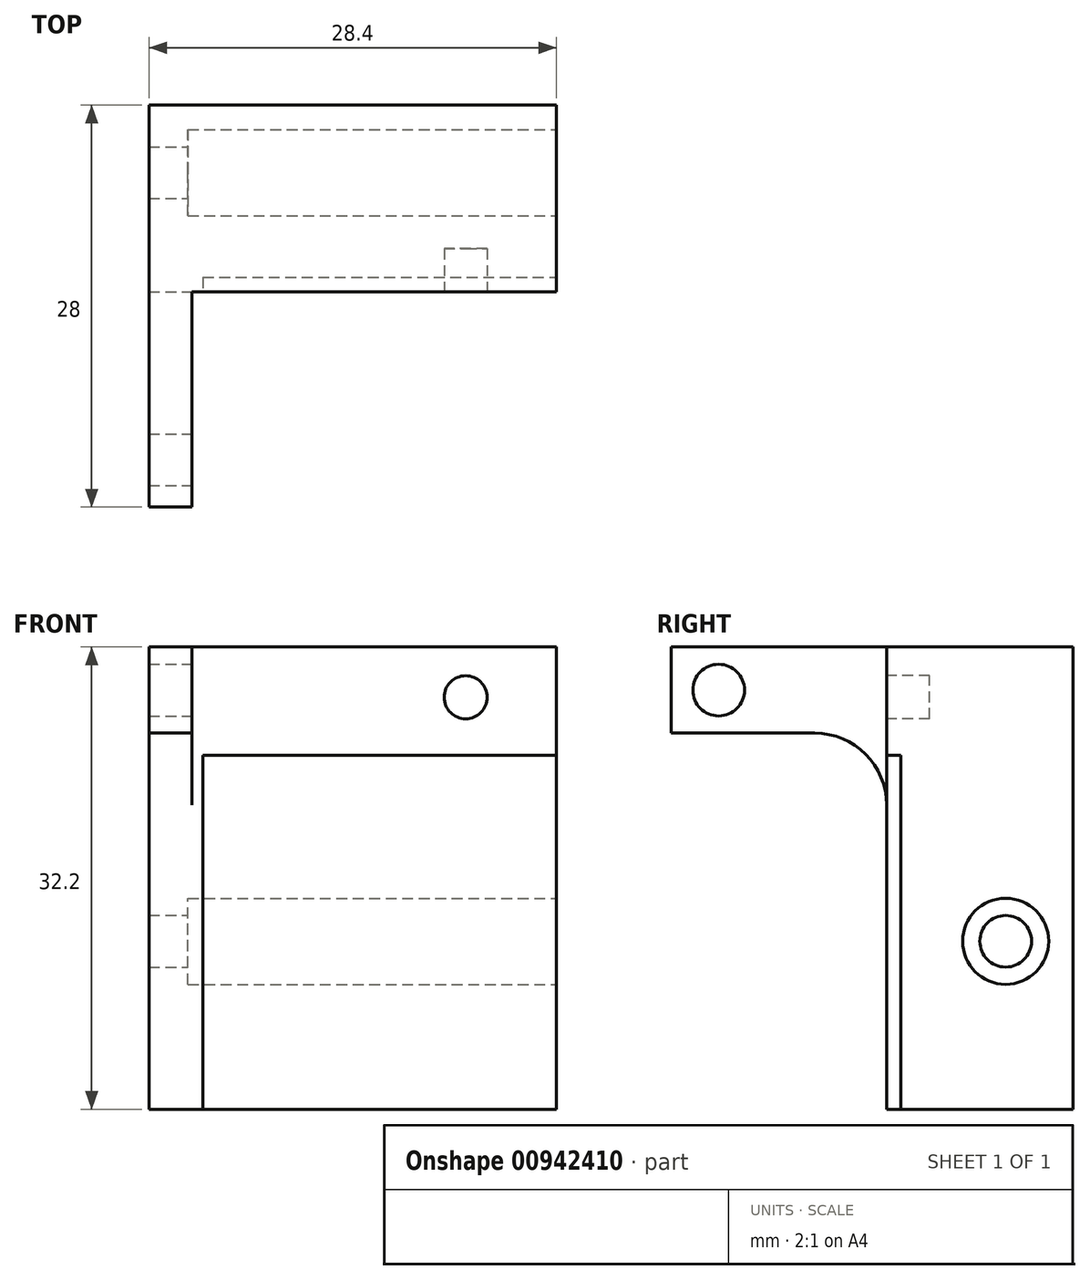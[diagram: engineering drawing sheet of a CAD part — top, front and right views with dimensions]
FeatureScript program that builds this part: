
annotation { "Feature Type Name" : "Feature", "Feature Type Description" : "" }
export const myFeature = defineFeature(function(context is Context, id is Id, definition is map)
    precondition{}
    {
        {
            var Q0;
            Q0=qCreatedBy(makeId("Front.planeOp"),FACE);
            var sketch = newSketch(context, id + "F0", { "sketchPlane" : qUnion([Q0])});
            skLineSegment(sketch, "E0.bottom", {"start": v(-15.2, 13.7) * mm, "end": v(15.2, 13.7) * mm});
            skLineSegment(sketch, "E0.top", {"start": v(-15.2, -13.7) * mm, "end": v(15.2, -13.7) * mm});
            skLineSegment(sketch, "E0.left", {"start": v(-15.2, 13.7) * mm, "end": v(-15.2, -13.7) * mm});
            skLineSegment(sketch, "E0.right", {"start": v(15.2, 13.7) * mm, "end": v(15.2, -13.7) * mm});
            skPoint(sketch, "E0.middle", {"position": v(0, 0) * mm});
            skSolve(sketch);
        }
        {
            var Q0;
            Q0 = qSketchRegion(id + "F0", true);
            extrude(context, id + "F1", {"entities" : qUnion([Q0]), "depth" : 3 * mm, "offsetDistance" : 25 * mm});
        }
        {
            var Q0;
            Q0=makeQuery(id+"F1.opExtrude","CAP_FACE",FACE,{"disambiguationData":[OSD([sQuery(id+"F0.wireOp",EDGE,"E0.bottom"),sQuery(id+"F0.wireOp",EDGE,"E0.top"),sQuery(id+"F0.wireOp",EDGE,"E0.left"),sQuery(id+"F0.wireOp",EDGE,"E0.right")])],"isStart":false});
            var sketch = newSketch(context, id + "F2", { "sketchPlane" : qUnion([Q0])});
            skLineSegment(sketch, "E1.bottom", {"start": v(-11.45, 12.95) * mm, "end": v(14.45, 12.95) * mm});
            skLineSegment(sketch, "E1.top", {"start": v(-11.45, -12.95) * mm, "end": v(14.45, -12.95) * mm});
            skLineSegment(sketch, "E1.left", {"start": v(-11.45, 12.95) * mm, "end": v(-11.45, -12.95) * mm});
            skLineSegment(sketch, "E1.right", {"start": v(14.45, 12.95) * mm, "end": v(14.45, -12.95) * mm});
            skSolve(sketch);
        }
        {
            var Q0;
            Q0 = qSketchRegion(id + "F2", true);
            extrude(context, id + "F3", {"entities" : qUnion([Q0]), "operationType" : NewBodyOperationType.REMOVE, "oppositeDirection" : true, "depth" : 1 * mm, "offsetDistance" : 25 * mm});
        }
        {
            var Q0;
            Q0=makeQuery(id+"F1.opExtrude","CAP_FACE",FACE,{"disambiguationData":[OSD([sQuery(id+"F0.wireOp",EDGE,"E0.bottom"),sQuery(id+"F0.wireOp",EDGE,"E0.top"),sQuery(id+"F0.wireOp",EDGE,"E0.left"),sQuery(id+"F0.wireOp",EDGE,"E0.right")])],"isStart":true});
            var sketch = newSketch(context, id + "F4", { "sketchPlane" : qUnion([Q0])});
            skLineSegment(sketch, "E2.bottom", {"start": v(12.2, 20.5) * mm, "end": v(15.2, 20.5) * mm});
            skLineSegment(sketch, "E2.top", {"start": v(12.2, -20.5) * mm, "end": v(15.2, -20.5) * mm});
            skLineSegment(sketch, "E2.left", {"start": v(12.2, 20.5) * mm, "end": v(12.2, -20.5) * mm});
            skLineSegment(sketch, "E2.right", {"start": v(15.2, 20.5) * mm, "end": v(15.2, -20.5) * mm});
            skSolve(sketch);
        }
        {
            var Q0;
            Q0 = qSketchRegion(id + "F4", true);
            extrude(context, id + "F5", {"entities" : qUnion([Q0]), "operationType" : NewBodyOperationType.ADD, "oppositeDirection" : true, "depth" : 18 * mm, "offsetDistance" : 25 * mm});
        }
        {
            var Q0;
            Q0=makeQuery(id+"F5.opExtrude","SWEPT_FACE",FACE,{"disambiguationData":[OSD([sQuery(id+"F4.wireOp",EDGE,"E2.left")])]});
            var sketch = newSketch(context, id + "F6", { "sketchPlane" : qUnion([Q0])});
            skLineSegment(sketch, "E3.bottom", {"start": v(-18, -14.5) * mm, "end": v(-8, -14.5) * mm});
            skLineSegment(sketch, "E3.top", {"start": v(-18, 14.5) * mm, "end": v(-8, 14.5) * mm});
            skLineSegment(sketch, "E3.left", {"start": v(-18, -14.5) * mm, "end": v(-18, 14.5) * mm});
            skLineSegment(sketch, "E3.right", {"start": v(-3, -9.5) * mm, "end": v(-3, 9.5) * mm});
            skPoint(sketch, "E4.visualSharp", {"position": v(-3, -14.5) * mm});
            skArc(sketch, "E4.filletArc", {"start": v(-8, -14.5) * mm, "mid": v(-4.46, -13.04) * mm, "end": v(-3, -9.5) * mm});
            skPoint(sketch, "E5.visualSharp", {"position": v(-3, 14.5) * mm});
            skArc(sketch, "E5.filletArc", {"start": v(-3, 9.5) * mm, "mid": v(-4.46, 13.04) * mm, "end": v(-8, 14.5) * mm});
            skSolve(sketch);
        }
        {
            var Q0;
            Q0 = qSketchRegion(id + "F6", true);
            extrude(context, id + "F7", {"entities" : qUnion([Q0]), "operationType" : NewBodyOperationType.REMOVE, "oppositeDirection" : true, "depth" : 25 * mm, "offsetDistance" : 25 * mm});
        }
        {
            var Q0;
            Q0=makeQuery(id+"F5.opExtrude","SWEPT_FACE",FACE,{"disambiguationData":[OSD([sQuery(id+"F4.wireOp",EDGE,"E2.left")])]});
            var sketch = newSketch(context, id + "F8", { "sketchPlane" : qUnion([Q0])});
            skCircle(sketch, "E6", {"center": v(-14.7, -17.5) * mm, "radius": 1.8 * mm});
            skPoint(sketch, "E6.centerSnap0", {"position": v(-18, -17.5) * mm});
            skCircle(sketch, "E7", {"center": v(-14.7, 17.5) * mm, "radius": 1.8 * mm});
            skPoint(sketch, "E7.centerSnap0", {"position": v(-18, 17.5) * mm});
            skSolve(sketch);
        }
        {
            var Q0;
            Q0 = qSketchRegion(id + "F8", true);
            extrude(context, id + "F9", {"entities" : qUnion([Q0]), "operationType" : NewBodyOperationType.REMOVE, "oppositeDirection" : true, "depth" : 25 * mm, "offsetDistance" : 25 * mm});
        }
        {
            var Q0;
            Q0=qCreatedBy(makeId("Front.planeOp"),FACE);
            var sketch = newSketch(context, id + "F10", { "sketchPlane" : qUnion([Q0])});
            skLineSegment(sketch, "E8.bottom", {"start": v(-12.2, 13.7) * mm, "end": v(15.2, 13.7) * mm});
            skLineSegment(sketch, "E8.top", {"start": v(-12.2, 20.5) * mm, "end": v(15.2, 20.5) * mm});
            skLineSegment(sketch, "E8.left", {"start": v(-12.2, 13.7) * mm, "end": v(-12.2, 20.5) * mm});
            skLineSegment(sketch, "E8.right", {"start": v(15.2, 13.7) * mm, "end": v(15.2, 20.5) * mm});
            skPoint(sketch, "E9.centerSnap0", {"position": v(15.2, 17.1) * mm});
            skSolve(sketch);
        }
        {
            var Q0;
            Q0 = qSketchRegion(id + "F10", true);
            extrude(context, id + "F11", {"entities" : qUnion([Q0]), "operationType" : NewBodyOperationType.ADD, "depth" : 3 * mm, "offsetDistance" : 25 * mm});
        }
        {
            var Q0;
            Q0=makeQuery(id+"F11.boolean.opBoolean","MERGE",FACE,{"derivedFrom":[makeQuery(id+"F7.boolean.opBoolean","MERGE",FACE,{"derivedFrom":[makeQuery(id+"F1.opExtrude","CAP_FACE",FACE,{"disambiguationData":[OSD([sQuery(id+"F0.wireOp",EDGE,"E0.bottom"),sQuery(id+"F0.wireOp",EDGE,"E0.top"),sQuery(id+"F0.wireOp",EDGE,"E0.left"),sQuery(id+"F0.wireOp",EDGE,"E0.right")])],"isStart":false})],"fromTools":[makeQuery(id+"F7.opExtrude","SWEPT_FACE",FACE,{"disambiguationData":[OSD([sQuery(id+"F6.wireOp",EDGE,"E3.right")])]})]}),makeQuery(id+"F11.opExtrude","CAP_FACE",FACE,{"disambiguationData":[OSD([sQuery(id+"F10.wireOp",EDGE,"E8.bottom"),sQuery(id+"F10.wireOp",EDGE,"E8.top"),sQuery(id+"F10.wireOp",EDGE,"E8.left"),sQuery(id+"F10.wireOp",EDGE,"E8.right")])],"isStart":false})]});
            var sketch = newSketch(context, id + "F12", { "sketchPlane" : qUnion([Q0])});
            skCircle(sketch, "E10", {"center": v(6.87, 17) * mm, "radius": 1.5 * mm});
            skSolve(sketch);
        }
        {
            var Q0;
            Q0 = qSketchRegion(id + "F12", true);
            extrude(context, id + "F13", {"entities" : qUnion([Q0]), "operationType" : NewBodyOperationType.REMOVE, "endBound" : BoundingType.THROUGH_ALL, "oppositeDirection" : true, "depth" : 62.4 * mm, "offsetDistance" : 25 * mm});
        }
        {
            var Q0;
            Q0=makeQuery(id+"F11.boolean.opBoolean","MERGE",FACE,{"derivedFrom":[makeQuery(id+"F7.boolean.opBoolean","MERGE",FACE,{"derivedFrom":[makeQuery(id+"F1.opExtrude","CAP_FACE",FACE,{"disambiguationData":[OSD([sQuery(id+"F0.wireOp",EDGE,"E0.bottom"),sQuery(id+"F0.wireOp",EDGE,"E0.top"),sQuery(id+"F0.wireOp",EDGE,"E0.left"),sQuery(id+"F0.wireOp",EDGE,"E0.right")])],"isStart":false})],"fromTools":[makeQuery(id+"F7.opExtrude","SWEPT_FACE",FACE,{"disambiguationData":[OSD([sQuery(id+"F6.wireOp",EDGE,"E3.right")])]})]}),makeQuery(id+"F11.opExtrude","CAP_FACE",FACE,{"disambiguationData":[OSD([sQuery(id+"F10.wireOp",EDGE,"E8.bottom"),sQuery(id+"F10.wireOp",EDGE,"E8.top"),sQuery(id+"F10.wireOp",EDGE,"E8.left"),sQuery(id+"F10.wireOp",EDGE,"E8.right")])],"isStart":false})]});
            var sketch = newSketch(context, id + "F14", { "sketchPlane" : qUnion([Q0])});
            skLineSegment(sketch, "E11.bottom", {"start": v(-12.2, -9.5) * mm, "end": v(-21.1, -9.5) * mm});
            skLineSegment(sketch, "E11.top", {"start": v(-12.2, -26.06) * mm, "end": v(-21.1, -26.06) * mm});
            skLineSegment(sketch, "E11.left", {"start": v(-12.2, -9.5) * mm, "end": v(-12.2, -26.06) * mm});
            skLineSegment(sketch, "E11.right", {"start": v(-21.1, -9.5) * mm, "end": v(-21.1, -26.06) * mm});
            skSolve(sketch);
        }
        {
            var Q0;
            Q0 = qSketchRegion(id + "F14", true);
            extrude(context, id + "F15", {"entities" : qUnion([Q0]), "operationType" : NewBodyOperationType.REMOVE, "depth" : 25 * mm, "offsetDistance" : 25 * mm});
        }
        {
            var Q0;
            Q0=makeQuery(id+"F15.boolean.opBoolean","MERGE",FACE,{"derivedFrom":[makeQuery(id+"F11.boolean.opBoolean","MERGE",FACE,{"derivedFrom":[makeQuery(id+"F7.boolean.opBoolean","MERGE",FACE,{"derivedFrom":[makeQuery(id+"F1.opExtrude","CAP_FACE",FACE,{"disambiguationData":[OSD([sQuery(id+"F0.wireOp",EDGE,"E0.bottom"),sQuery(id+"F0.wireOp",EDGE,"E0.top"),sQuery(id+"F0.wireOp",EDGE,"E0.left"),sQuery(id+"F0.wireOp",EDGE,"E0.right")])],"isStart":false})],"fromTools":[makeQuery(id+"F7.opExtrude","SWEPT_FACE",FACE,{"disambiguationData":[OSD([sQuery(id+"F6.wireOp",EDGE,"E3.right")])]})]}),makeQuery(id+"F11.opExtrude","CAP_FACE",FACE,{"disambiguationData":[OSD([sQuery(id+"F10.wireOp",EDGE,"E8.bottom"),sQuery(id+"F10.wireOp",EDGE,"E8.top"),sQuery(id+"F10.wireOp",EDGE,"E8.left"),sQuery(id+"F10.wireOp",EDGE,"E8.right")])],"isStart":false})]})],"fromTools":[makeQuery(id+"F15.opExtrude","CAP_FACE",FACE,{"disambiguationData":[OSD([sQuery(id+"F14.wireOp",EDGE,"E11.bottom"),sQuery(id+"F14.wireOp",EDGE,"E11.top"),sQuery(id+"F14.wireOp",EDGE,"E11.left"),sQuery(id+"F14.wireOp",EDGE,"E11.right")])],"isStart":true})]});
            var sketch = newSketch(context, id + "F16", { "sketchPlane" : qUnion([Q0])});
            skLineSegment(sketch, "E12.bottom", {"start": v(-12.2, -13.7) * mm, "end": v(-21.3, -13.7) * mm});
            skLineSegment(sketch, "E12.top", {"start": v(-12.2, -25.88) * mm, "end": v(-21.3, -25.88) * mm});
            skLineSegment(sketch, "E12.left", {"start": v(-12.2, -13.7) * mm, "end": v(-12.2, -25.88) * mm});
            skLineSegment(sketch, "E12.right", {"start": v(-21.3, -13.7) * mm, "end": v(-21.3, -25.88) * mm});
            skSolve(sketch);
        }
        {
            var Q0;
            Q0 = qSketchRegion(id + "F16", true);
            extrude(context, id + "F17", {"entities" : qUnion([Q0]), "operationType" : NewBodyOperationType.REMOVE, "oppositeDirection" : true, "depth" : 25 * mm, "offsetDistance" : 25 * mm});
        }
        {
            var Q0;
            Q0=makeQuery(id+"F15.boolean.opBoolean","MERGE",FACE,{"derivedFrom":[makeQuery(id+"F11.boolean.opBoolean","MERGE",FACE,{"derivedFrom":[makeQuery(id+"F7.boolean.opBoolean","MERGE",FACE,{"derivedFrom":[makeQuery(id+"F1.opExtrude","CAP_FACE",FACE,{"disambiguationData":[OSD([sQuery(id+"F0.wireOp",EDGE,"E0.bottom"),sQuery(id+"F0.wireOp",EDGE,"E0.top"),sQuery(id+"F0.wireOp",EDGE,"E0.left"),sQuery(id+"F0.wireOp",EDGE,"E0.right")])],"isStart":false})],"fromTools":[makeQuery(id+"F7.opExtrude","SWEPT_FACE",FACE,{"disambiguationData":[OSD([sQuery(id+"F6.wireOp",EDGE,"E3.right")])]})]}),makeQuery(id+"F11.opExtrude","CAP_FACE",FACE,{"disambiguationData":[OSD([sQuery(id+"F10.wireOp",EDGE,"E8.bottom"),sQuery(id+"F10.wireOp",EDGE,"E8.top"),sQuery(id+"F10.wireOp",EDGE,"E8.left"),sQuery(id+"F10.wireOp",EDGE,"E8.right")])],"isStart":false})]})],"fromTools":[makeQuery(id+"F15.opExtrude","CAP_FACE",FACE,{"disambiguationData":[OSD([sQuery(id+"F14.wireOp",EDGE,"E11.bottom"),sQuery(id+"F14.wireOp",EDGE,"E11.top"),sQuery(id+"F14.wireOp",EDGE,"E11.left"),sQuery(id+"F14.wireOp",EDGE,"E11.right")])],"isStart":true})]});
            var sketch = newSketch(context, id + "F18", { "sketchPlane" : qUnion([Q0])});
            skLineSegment(sketch, "E13.bottom", {"start": v(13.2, 20.5) * mm, "end": v(15.2, 20.5) * mm});
            skLineSegment(sketch, "E13.top", {"start": v(13.2, -16.6) * mm, "end": v(15.2, -16.6) * mm});
            skLineSegment(sketch, "E13.left", {"start": v(13.2, 20.5) * mm, "end": v(13.2, -16.6) * mm});
            skLineSegment(sketch, "E13.right", {"start": v(15.2, 20.5) * mm, "end": v(15.2, -16.6) * mm});
            skSolve(sketch);
        }
        {
            var Q0;
            Q0 = qSketchRegion(id + "F18", true);
            extrude(context, id + "F19", {"entities" : qUnion([Q0]), "operationType" : NewBodyOperationType.REMOVE, "oppositeDirection" : true, "depth" : 25 * mm, "offsetDistance" : 25 * mm});
        }
        {
            var Q0;
            Q0=makeQuery(id+"F11.boolean.opBoolean","MERGE",FACE,{"derivedFrom":[makeQuery(id+"F5.boolean.opBoolean","MERGE",FACE,{"derivedFrom":[makeQuery(id+"F1.opExtrude","CAP_FACE",FACE,{"disambiguationData":[OSD([sQuery(id+"F0.wireOp",EDGE,"E0.bottom"),sQuery(id+"F0.wireOp",EDGE,"E0.top"),sQuery(id+"F0.wireOp",EDGE,"E0.left"),sQuery(id+"F0.wireOp",EDGE,"E0.right")])],"isStart":true}),makeQuery(id+"F5.opExtrude","CAP_FACE",FACE,{"disambiguationData":[OSD([sQuery(id+"F4.wireOp",EDGE,"E2.bottom"),sQuery(id+"F4.wireOp",EDGE,"E2.top"),sQuery(id+"F4.wireOp",EDGE,"E2.left"),sQuery(id+"F4.wireOp",EDGE,"E2.right")])],"isStart":true})]}),makeQuery(id+"F11.opExtrude","CAP_FACE",FACE,{"disambiguationData":[OSD([sQuery(id+"F10.wireOp",EDGE,"E8.bottom"),sQuery(id+"F10.wireOp",EDGE,"E8.top"),sQuery(id+"F10.wireOp",EDGE,"E8.left"),sQuery(id+"F10.wireOp",EDGE,"E8.right")])],"isStart":true})]});
            var sketch = newSketch(context, id + "F20", { "sketchPlane" : qUnion([Q0])});
            skLineSegment(sketch, "E14.bottom", {"start": v(-13.2, -13.7) * mm, "end": v(15.2, -13.7) * mm});
            skLineSegment(sketch, "E14.top", {"start": v(-13.2, 20.5) * mm, "end": v(15.2, 20.5) * mm});
            skLineSegment(sketch, "E14.left", {"start": v(-13.2, -13.7) * mm, "end": v(-13.2, 20.5) * mm});
            skLineSegment(sketch, "E14.right", {"start": v(15.2, -13.7) * mm, "end": v(15.2, 20.5) * mm});
            skSolve(sketch);
        }
        {
            var Q0;
            Q0 = qSketchRegion(id + "F20", true);
            extrude(context, id + "F21", {"entities" : qUnion([Q0]), "operationType" : NewBodyOperationType.ADD, "depth" : 10 * mm, "offsetDistance" : 25 * mm});
        }
        {
            var Q0;
            Q0=makeQuery(id+"F21.boolean.opBoolean","MERGE",FACE,{"derivedFrom":[makeQuery(id+"F19.boolean.opBoolean","COPY",FACE,{"derivedFrom":makeQuery(id+"F19.opExtrude","SWEPT_FACE",FACE,{"disambiguationData":[OSD([sQuery(id+"F18.wireOp",EDGE,"E13.left")])]})}),makeQuery(id+"F21.opExtrude","SWEPT_FACE",FACE,{"disambiguationData":[OSD([sQuery(id+"F20.wireOp",EDGE,"E14.left")])]})]});
            var sketch = newSketch(context, id + "F22", { "sketchPlane" : qUnion([Q0])});
            skCircle(sketch, "E15", {"center": v(5.3, 0) * mm, "radius": 1.8 * mm});
            skCircle(sketch, "E16", {"center": v(-14.7, 17.5) * mm, "radius": 2.41 * mm, "construction": true});
            skSolve(sketch);
        }
        {
            var Q0;
            Q0 = qSketchRegion(id + "F22", true);
            extrude(context, id + "F23", {"entities" : qUnion([Q0]), "operationType" : NewBodyOperationType.REMOVE, "oppositeDirection" : true, "depth" : 38.7 * mm, "offsetDistance" : 25 * mm});
        }
        {
            var Q0;
            Q0=makeQuery(id+"F21.boolean.opBoolean","MERGE",FACE,{"derivedFrom":[makeQuery(id+"F19.boolean.opBoolean","COPY",FACE,{"derivedFrom":makeQuery(id+"F19.opExtrude","SWEPT_FACE",FACE,{"disambiguationData":[OSD([sQuery(id+"F18.wireOp",EDGE,"E13.left")])]})}),makeQuery(id+"F21.opExtrude","SWEPT_FACE",FACE,{"disambiguationData":[OSD([sQuery(id+"F20.wireOp",EDGE,"E14.left")])]})]});
            var sketch = newSketch(context, id + "F24", { "sketchPlane" : qUnion([Q0])});
            skCircle(sketch, "E17", {"center": v(5.3, 0) * mm, "radius": 3 * mm});
            skSolve(sketch);
        }
        {
            var Q0;
            Q0 = qSketchRegion(id + "F24", true);
            extrude(context, id + "F25", {"entities" : qUnion([Q0]), "operationType" : NewBodyOperationType.REMOVE, "oppositeDirection" : true, "depth" : 25.7 * mm, "offsetDistance" : 25 * mm});
        }
        {
            var Q0;
            Q0=makeQuery(id+"F15.boolean.opBoolean","MERGE",FACE,{"derivedFrom":[makeQuery(id+"F11.boolean.opBoolean","MERGE",FACE,{"derivedFrom":[makeQuery(id+"F7.boolean.opBoolean","MERGE",FACE,{"derivedFrom":[makeQuery(id+"F1.opExtrude","CAP_FACE",FACE,{"disambiguationData":[OSD([sQuery(id+"F0.wireOp",EDGE,"E0.bottom"),sQuery(id+"F0.wireOp",EDGE,"E0.top"),sQuery(id+"F0.wireOp",EDGE,"E0.left"),sQuery(id+"F0.wireOp",EDGE,"E0.right")])],"isStart":false})],"fromTools":[makeQuery(id+"F7.opExtrude","SWEPT_FACE",FACE,{"disambiguationData":[OSD([sQuery(id+"F6.wireOp",EDGE,"E3.right")])]})]}),makeQuery(id+"F11.opExtrude","CAP_FACE",FACE,{"disambiguationData":[OSD([sQuery(id+"F10.wireOp",EDGE,"E8.bottom"),sQuery(id+"F10.wireOp",EDGE,"E8.top"),sQuery(id+"F10.wireOp",EDGE,"E8.left"),sQuery(id+"F10.wireOp",EDGE,"E8.right")])],"isStart":false})]})],"fromTools":[makeQuery(id+"F15.opExtrude","CAP_FACE",FACE,{"disambiguationData":[OSD([sQuery(id+"F14.wireOp",EDGE,"E11.bottom"),sQuery(id+"F14.wireOp",EDGE,"E11.top"),sQuery(id+"F14.wireOp",EDGE,"E11.left"),sQuery(id+"F14.wireOp",EDGE,"E11.right")])],"isStart":true})]});
            var sketch = newSketch(context, id + "F26", { "sketchPlane" : qUnion([Q0])});
            skLineSegment(sketch, "E18.bottom", {"start": v(-11.45, -12.95) * mm, "end": v(14.43, -12.95) * mm});
            skLineSegment(sketch, "E18.top", {"start": v(-11.45, -18.8) * mm, "end": v(14.43, -18.8) * mm});
            skLineSegment(sketch, "E18.left", {"start": v(-11.45, -12.95) * mm, "end": v(-11.45, -18.8) * mm});
            skLineSegment(sketch, "E18.right", {"start": v(14.43, -12.95) * mm, "end": v(14.43, -18.8) * mm});
            skSolve(sketch);
        }
        {
            var Q0;
            Q0 = qSketchRegion(id + "F26", true);
            extrude(context, id + "F27", {"entities" : qUnion([Q0]), "operationType" : NewBodyOperationType.REMOVE, "oppositeDirection" : true, "depth" : 1 * mm, "offsetDistance" : 25 * mm});
        }
        {
            var Q0;
            Q0=makeQuery(id+"F15.boolean.opBoolean","MERGE",FACE,{"derivedFrom":[makeQuery(id+"F11.boolean.opBoolean","MERGE",FACE,{"derivedFrom":[makeQuery(id+"F7.boolean.opBoolean","MERGE",FACE,{"derivedFrom":[makeQuery(id+"F1.opExtrude","CAP_FACE",FACE,{"disambiguationData":[OSD([sQuery(id+"F0.wireOp",EDGE,"E0.bottom"),sQuery(id+"F0.wireOp",EDGE,"E0.top"),sQuery(id+"F0.wireOp",EDGE,"E0.left"),sQuery(id+"F0.wireOp",EDGE,"E0.right")])],"isStart":false})],"fromTools":[makeQuery(id+"F7.opExtrude","SWEPT_FACE",FACE,{"disambiguationData":[OSD([sQuery(id+"F6.wireOp",EDGE,"E3.right")])]})]}),makeQuery(id+"F11.opExtrude","CAP_FACE",FACE,{"disambiguationData":[OSD([sQuery(id+"F10.wireOp",EDGE,"E8.bottom"),sQuery(id+"F10.wireOp",EDGE,"E8.top"),sQuery(id+"F10.wireOp",EDGE,"E8.left"),sQuery(id+"F10.wireOp",EDGE,"E8.right")])],"isStart":false})]})],"fromTools":[makeQuery(id+"F15.opExtrude","CAP_FACE",FACE,{"disambiguationData":[OSD([sQuery(id+"F14.wireOp",EDGE,"E11.bottom"),sQuery(id+"F14.wireOp",EDGE,"E11.top"),sQuery(id+"F14.wireOp",EDGE,"E11.left"),sQuery(id+"F14.wireOp",EDGE,"E11.right")])],"isStart":true})]});
            var sketch = newSketch(context, id + "F28", { "sketchPlane" : qUnion([Q0])});
            skLineSegment(sketch, "E19.bottom", {"start": v(-15.2, -13.7) * mm, "end": v(46.56, -13.7) * mm});
            skLineSegment(sketch, "E19.top", {"start": v(-15.2, -11.7) * mm, "end": v(46.56, -11.7) * mm});
            skLineSegment(sketch, "E19.left", {"start": v(-15.2, -13.7) * mm, "end": v(-15.2, -11.7) * mm});
            skLineSegment(sketch, "E19.right", {"start": v(46.56, -13.7) * mm, "end": v(46.56, -11.7) * mm});
            skSolve(sketch);
        }
        {
            var Q0;
            Q0 = qSketchRegion(id + "F28", true);
            extrude(context, id + "F29", {"entities" : qUnion([Q0]), "operationType" : NewBodyOperationType.REMOVE, "oppositeDirection" : true, "depth" : 25 * mm, "offsetDistance" : 25 * mm});
        }
    });
